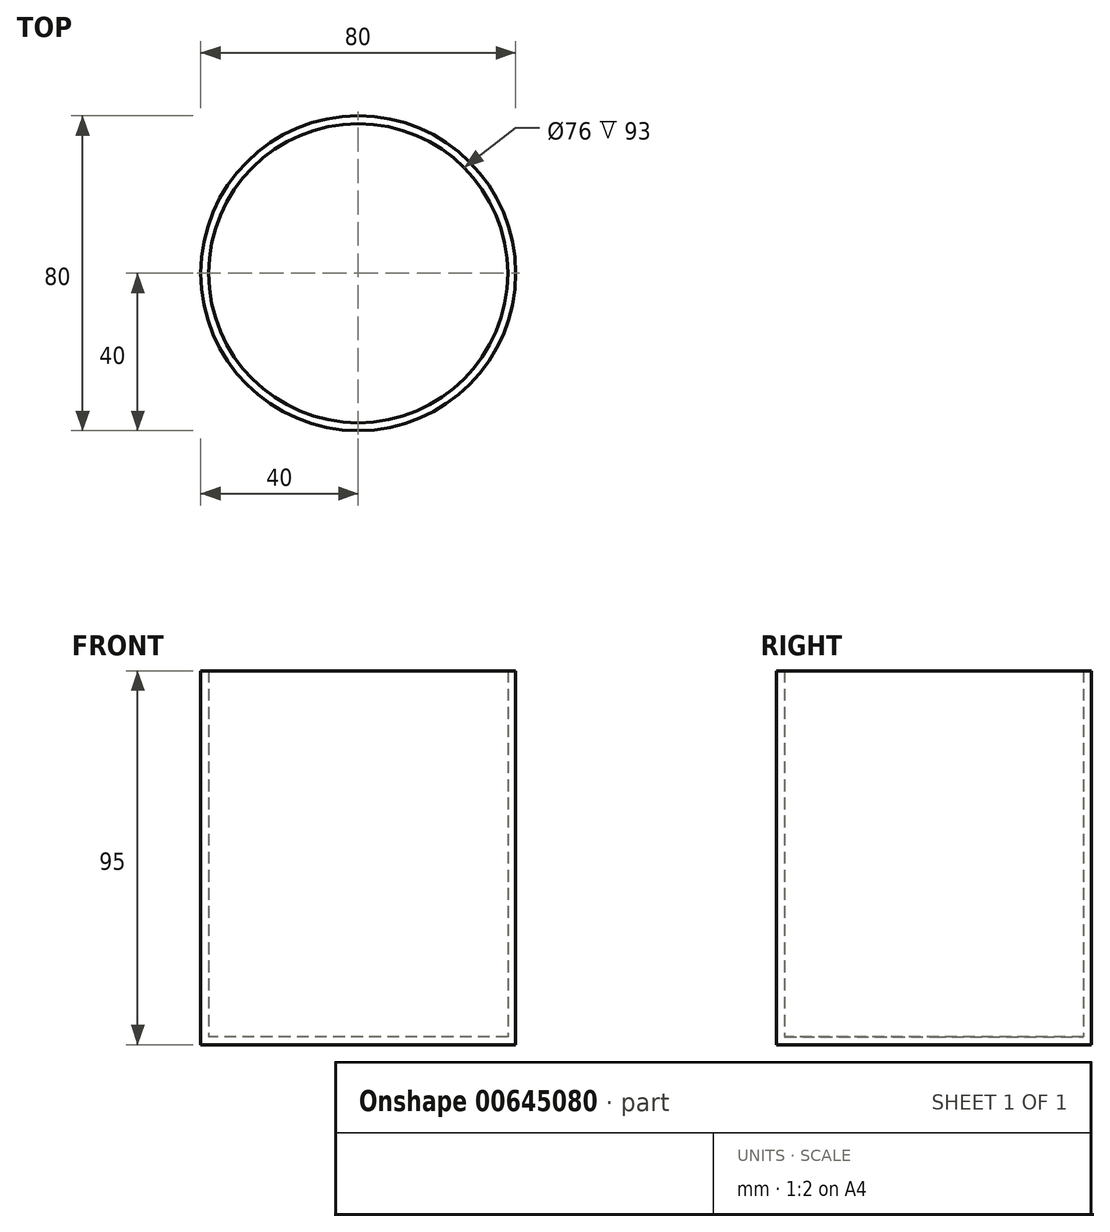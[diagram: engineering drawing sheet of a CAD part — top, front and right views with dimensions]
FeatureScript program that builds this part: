
annotation { "Feature Type Name" : "Feature", "Feature Type Description" : "" }
export const myFeature = defineFeature(function(context is Context, id is Id, definition is map)
    precondition{}
    {
        {
            var Q0;
            Q0=qCreatedBy(makeId("Top.planeOp"),FACE);
            var sketch = newSketch(context, id + "F0", { "sketchPlane" : qUnion([Q0])});
            skCircle(sketch, "E0", {"center": v(0, 0) * mm, "radius": 40 * mm});
            skSolve(sketch);
        }
        {
            var Q0;
            Q0 = qSketchRegion(id + "F0", true);
            extrude(context, id + "F1", {"entities" : qUnion([Q0]), "depth" : 95 * mm, "offsetDistance" : 25 * mm});
        }
        {
            var Q0;
            Q0=makeQuery(id+"F1.opExtrude","CAP_FACE",FACE,{"disambiguationData":[OSD([sQuery(id+"F0.wireOp",EDGE,"E0")])],"isStart":false});
            shell(context, id + "F2", {"entities" : qUnion([Q0]), "thickness" : 2 * mm});
        }
        {
            var Q0;
            Q0=qCreatedBy(makeId("Front.planeOp"),FACE);
            var sketch = newSketch(context, id + "F3", { "sketchPlane" : qUnion([Q0])});
            skFitSpline(sketch, "E1", {"points": [v(35.04, 77.63) * mm, v(47.4, 78.27) * mm, v(60.6, 81.68) * mm, v(68.9, 76.35) * mm, v(87.23, 72.52) * mm, v(89.57, 62.5) * mm, v(80.41, 34.18) * mm, v(72.32, 16.5) * mm, v(66.14, 25.87) * mm, v(60.39, 18.84) * mm, v(58.04, 10.75) * mm, v(50.16, 10.96) * mm, v(45.26, 16.5) * mm, v(35.9, 16.92) * mm], "startDerivative": vector(154.28, -10.66) * mm, "endDerivative": vector(-161.22, -22.47) * mm});
            skSolve(sketch);
        }
        {
            var Q0;
            Q0=qCreatedBy(makeId("Right.planeOp"),FACE);
            cPlane(context, id + "F4", {"entities" : qUnion([Q0]), "cplaneType" : CPlaneType.OFFSET, "offset" : 39 * mm, "width" : 150 * mm, "height" : 150 * mm});
        }
        {
            var Q0;
            Q0=qCreatedBy(id+"F4.planeOp",FACE);
            var sketch = newSketch(context, id + "F5", { "sketchPlane" : qUnion([Q0])});
            skCircle(sketch, "E2", {"center": v(0, 16.07) * mm, "radius": 4.62 * mm});
            skSolve(sketch);
        }
    });
